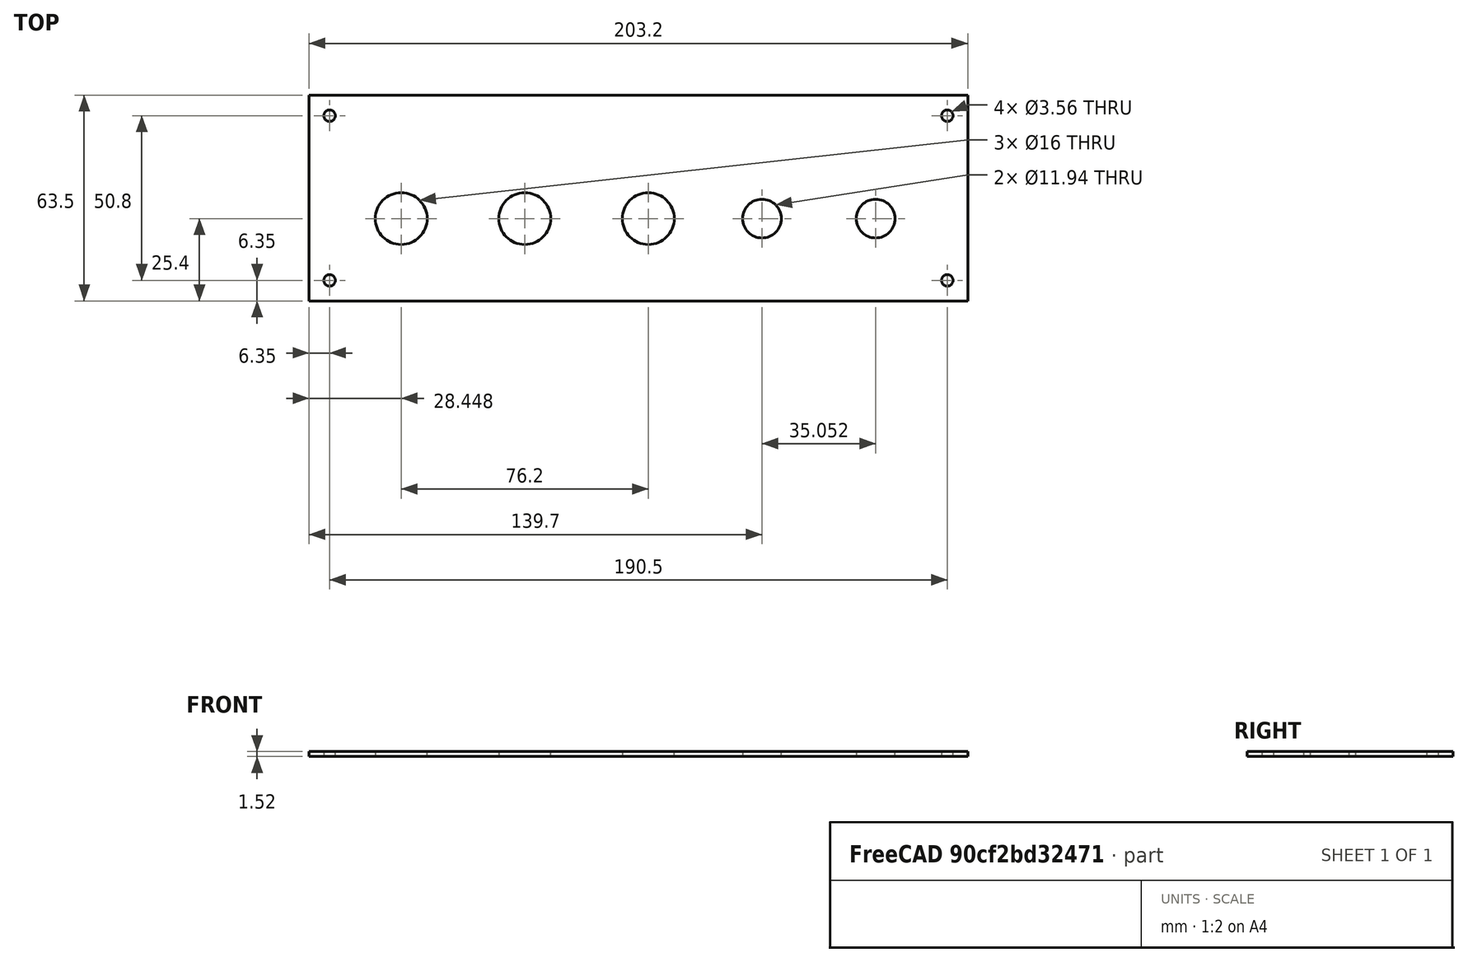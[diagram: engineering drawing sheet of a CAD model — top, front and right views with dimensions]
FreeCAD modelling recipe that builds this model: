
FCSTD DOCUMENT  (FreeCAD 1.1R20260414 (Git shallow))
Label: aluminum-bottom-panel
License: All rights reserved
LicenseURL: https://en.wikipedia.org/wiki/All_rights_reserved
objects: App::Point×1, Sketcher::SketchObject×1, PartDesign::Pad×1, PartDesign::Body×1
note: 6 computed .brp shape members not serialized (recipe doc carries the construction recipe); baked Part::Feature solids carry a one-line shape summary decoded from their .brp

FEATURE [App::Point] Origin001
  Role = Origin
FEATURE [Sketcher::SketchObject] Sketch
  ArcFitTolerance = 1e-06
  AttachmentSupport = -> [Origin]
  ExternalTypes = [0]
  FullyConstrained = true
  MakeInternals = false
  MapMode = 5
  _ExternalGeoVersion = 1
  sketch-geometry (21):
    g0: LineSegment StartX=0 StartY=31.75 StartZ=0 EndX=0 EndY=-31.75 EndZ=0
    g1: LineSegment StartX=0 StartY=-31.75 StartZ=0 EndX=203.2 EndY=-31.75 EndZ=0
    g2: LineSegment StartX=203.2 StartY=-31.75 StartZ=0 EndX=203.2 EndY=31.75 EndZ=0
    g3: LineSegment StartX=203.2 StartY=31.75 StartZ=0 EndX=0 EndY=31.75 EndZ=0
    g4: Circle CenterX=28.448 CenterY=-6.35 CenterZ=0 NormalX=0 NormalY=0 NormalZ=1 AngleXU=0 Radius=8.001
    g5: Circle CenterX=66.548 CenterY=-6.35 CenterZ=0 NormalX=0 NormalY=0 NormalZ=1 AngleXU=0 Radius=8.001
    g6: Circle CenterX=104.648 CenterY=-6.35 CenterZ=0 NormalX=0 NormalY=0 NormalZ=1 AngleXU=0 Radius=8.001
    g7: Circle CenterX=139.7 CenterY=-6.35 CenterZ=0 NormalX=0 NormalY=0 NormalZ=1 AngleXU=0 Radius=5.969
    g8: Circle CenterX=174.752 CenterY=-6.35 CenterZ=0 NormalX=0 NormalY=0 NormalZ=1 AngleXU=0 Radius=5.969
    g9: Circle CenterX=196.85 CenterY=-25.4 CenterZ=0 NormalX=0 NormalY=0 NormalZ=1 AngleXU=0 Radius=1.778
    g10: Circle CenterX=196.85 CenterY=25.4 CenterZ=0 NormalX=0 NormalY=0 NormalZ=1 AngleXU=0 Radius=1.778
    g11: Circle CenterX=6.35 CenterY=-25.4 CenterZ=0 NormalX=0 NormalY=0 NormalZ=1 AngleXU=0 Radius=1.778
    g12: Circle CenterX=6.35 CenterY=25.4 CenterZ=0 NormalX=0 NormalY=0 NormalZ=1 AngleXU=0 Radius=1.778
    g13: GeomPoint X=101.6 Y=-8e-16 Z=0
    g14: LineSegment [constr] StartX=101.6 StartY=31.75 StartZ=0 EndX=101.6 EndY=-31.75 EndZ=0
    g15: LineSegment [constr] StartX=28.448 StartY=-6.35 StartZ=0 EndX=66.548 EndY=-6.35 EndZ=0
    g16: LineSegment [constr] StartX=66.548 StartY=-6.35 StartZ=0 EndX=104.648 EndY=-6.35 EndZ=0
    g17: LineSegment [constr] StartX=104.648 StartY=-6.35 StartZ=0 EndX=139.7 EndY=-6.35 EndZ=0
    g18: LineSegment [constr] StartX=139.7 StartY=-6.35 StartZ=0 EndX=174.752 EndY=-6.35 EndZ=0
    g19: LineSegment [constr] StartX=28.448 StartY=-6.35 StartZ=0 EndX=0 EndY=-6.35 EndZ=0
    g20: LineSegment [constr] StartX=174.752 StartY=-6.35 StartZ=0 EndX=203.2 EndY=-6.35 EndZ=0
  constraints (54):
    c: Coincident(g0,g1)
    c: Coincident(g1,g2)
    c: Coincident(g2,g3)
    c: Coincident(g3,g0)
    c: Vertical(g2)
    c: Horizontal(g1)
    c: Horizontal(g3)
    c: PointOnObject(g0,g-2)
    c: DistanceX(g3,g3) = 203.2
    c: DistanceY(g2,g2) = 63.5
    c: Equal(g4,g5)
    c: Equal(g5,g6)
    c: Equal(g7,g8)
    c: Diameter(g7) = 11.938
    c: Diameter(g4) = 16.002
    c: DistanceX(g4,g5) = 38.1
    c: Horizontal(g8,g7)
    c: DistanceX(g-1,g4) = 28.448
    c: Vertical(g12,g11)
    c: Equal(g11,g12)
    c: Equal(g12,g10)
    c: Equal(g10,g9)
    c: Diameter(g10) = 3.556
    c: Horizontal(g12,g10)
    c: DistanceY(g10,g2) = 6.35
    c: DistanceX(g10,g2) = 6.35
    c: Symmetric(g9,g10,g-1)
    c: Symmetric(g1,g0,g13)
    c: Symmetric(g3,g3,g14)
    c: Symmetric(g1,g1,g14)
    c: Symmetric(g11,g9,g14)
    c: Horizontal(g4,g5)
    c: Horizontal(g5,g6)
    c: Horizontal(g6,g7)
    c: Coincident(g15,g4)
    c: Coincident(g15,g5)
    c: Coincident(g16,g5)
    c: Coincident(g16,g6)
    c: Coincident(g17,g6)
    c: Coincident(g17,g7)
    c: Coincident(g18,g7)
    c: Coincident(g18,g8)
    c: Equal(g15,g16)
    c: DistanceY(g0,g4) = 25.4
    c: Symmetric(g0,g0,g-1)
    c: Coincident(g19,g4)
    c: PointOnObject(g19,g0)
    c: Horizontal(g19)
    c: Coincident(g20,g8)
    c: PointOnObject(g20,g2)
    c: Horizontal(g20)
    c: Equal(g20,g19)
    c: Equal(g17,g18)
    c: DistanceX(g7,g8) = 35.052
FEATURE [PartDesign::Pad] Pad
  Direction = (0,0,1)
  Length = 1.524
  Length2 = 10
  Profile = -> Sketch
  ReferenceAxis = -> Sketch [N_Axis]
  Refine = true
  SideType = 0
  Suppressed = false
  Type = 0
  Type2 = 0
FEATURE [PartDesign::Body] Body
  AllowCompound = false
  Group = -> [Sketch,Pad]
  Origin = -> Origin
  Tip = -> Pad
